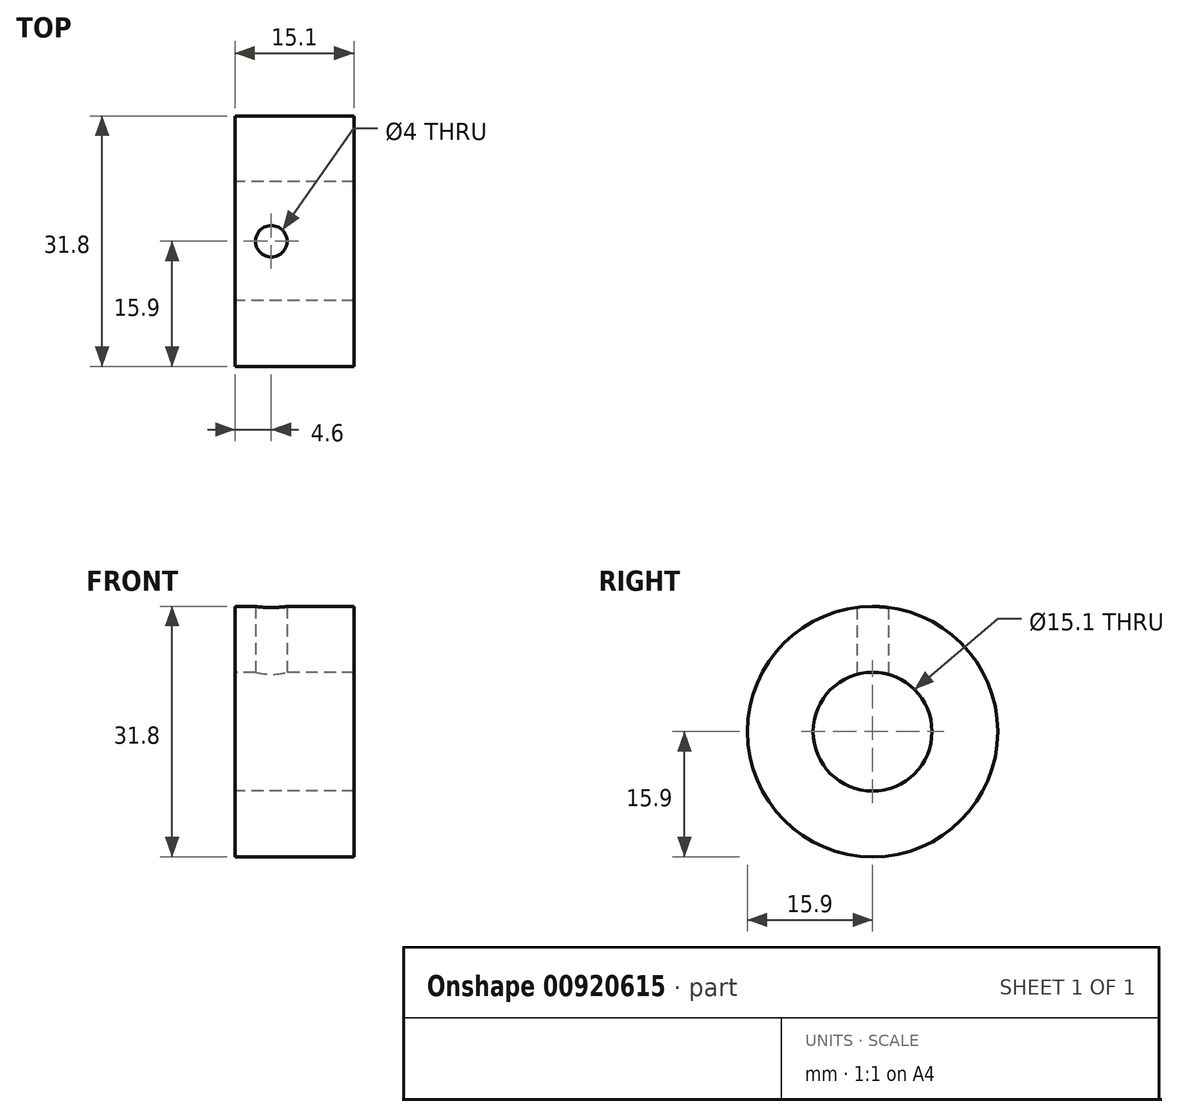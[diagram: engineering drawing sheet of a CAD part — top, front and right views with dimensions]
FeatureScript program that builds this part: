
annotation { "Feature Type Name" : "Feature", "Feature Type Description" : "" }
export const myFeature = defineFeature(function(context is Context, id is Id, definition is map)
    precondition{}
    {
        {
            var Q0;
            Q0=qCreatedBy(makeId("Front.planeOp"),FACE);
            var sketch = newSketch(context, id + "F0", { "sketchPlane" : qUnion([Q0])});
            skLineSegment(sketch, "E0", {"start": v(-14.76, 0) * mm, "end": v(14.3, 0) * mm, "construction": true});
            skLineSegment(sketch, "E1.bottom", {"start": v(0, 7.55) * mm, "end": v(-15.1, 7.55) * mm});
            skLineSegment(sketch, "E1.top", {"start": v(0, 15.9) * mm, "end": v(-15.1, 15.9) * mm});
            skLineSegment(sketch, "E1.left", {"start": v(0, 7.55) * mm, "end": v(0, 15.9) * mm});
            skLineSegment(sketch, "E1.right", {"start": v(-15.1, 7.55) * mm, "end": v(-15.1, 15.9) * mm});
            skSolve(sketch);
        }
        {
            var Q0;
            Q0=makeQuery(id+"F0.imprint","IMPRINT",FACE,{"disambiguationData":[TD([[makeQuery(id+"F0.imprint","IMPRINT",EDGE,{"derivedFrom":sQuery(id+"F0.wireOp",EDGE,"E1.bottom")}),-1.0]])]});
            var Q1;
            Q1=sQuery(id+"F0.wireOp",EDGE,"E0");
            revolve(context, id + "F1", {"surfaceOperationType" : NewSurfaceOperationType.NEW, "entities" : qUnion([Q0]), "axis" : qUnion([Q1]), "revolveType" : RevolveType.FULL});
        }
        {
            var Q0;
            Q0=qCreatedBy(makeId("Top.planeOp"),FACE);
            var sketch = newSketch(context, id + "F2", { "sketchPlane" : qUnion([Q0])});
            skCircle(sketch, "E2", {"center": v(-10.5, 0) * mm, "radius": 2 * mm});
            skSolve(sketch);
        }
        {
            var Q0;
            Q0=makeQuery(id+"F2.imprint","IMPRINT",FACE,{"disambiguationData":[TD([[makeQuery(id+"F2.imprint","IMPRINT",EDGE,{"derivedFrom":sQuery(id+"F2.wireOp",EDGE,"E2")}),1.0]])]});
            extrude(context, id + "F3", {"entities" : qUnion([Q0]), "operationType" : NewBodyOperationType.REMOVE, "depth" : 25 * mm, "offsetDistance" : 25 * mm});
        }
    });
